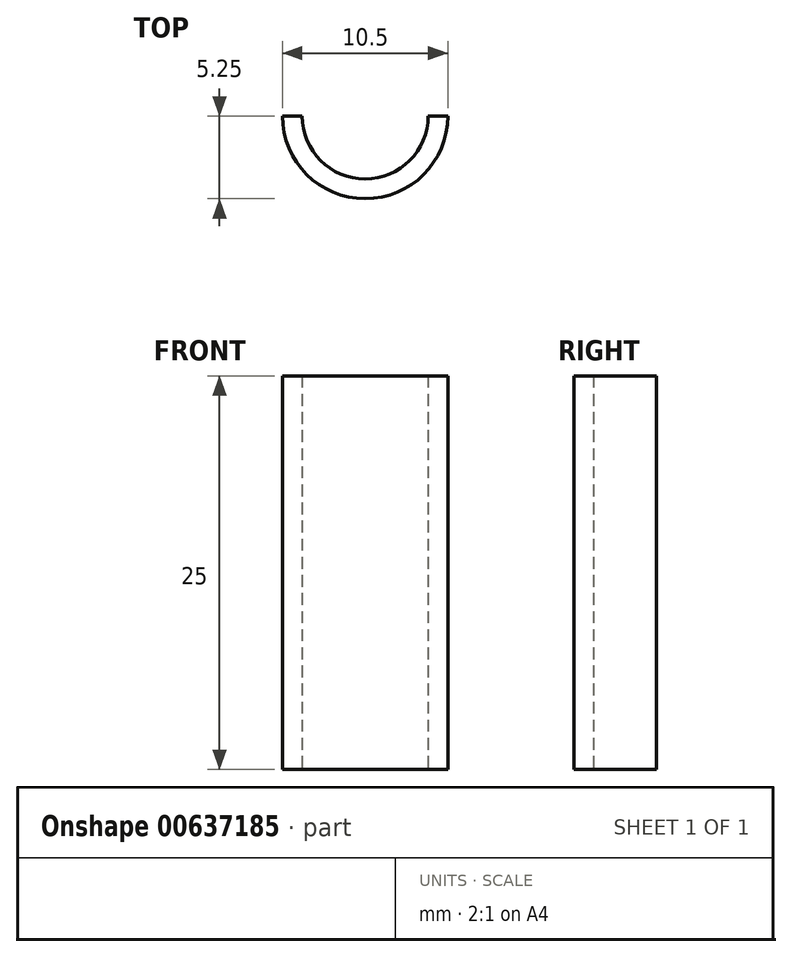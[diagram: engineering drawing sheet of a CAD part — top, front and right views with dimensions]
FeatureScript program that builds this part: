
annotation { "Feature Type Name" : "Feature", "Feature Type Description" : "" }
export const myFeature = defineFeature(function(context is Context, id is Id, definition is map)
    precondition{}
    {
        {
            var Q0;
            Q0=qCreatedBy(makeId("Top.planeOp"),FACE);
            var sketch = newSketch(context, id + "F0", { "sketchPlane" : qUnion([Q0])});
            skArc(sketch, "E0", {"start": v(-4, 0) * mm, "mid": v(0, -4) * mm, "end": v(4, 0) * mm});
            skArc(sketch, "E1", {"start": v(-5.25, 0) * mm, "mid": v(0, -5.25) * mm, "end": v(5.25, 0) * mm});
            skLineSegment(sketch, "E2", {"start": v(-4, 0) * mm, "end": v(-5.25, 0) * mm});
            skLineSegment(sketch, "E3", {"start": v(-5.25, 0) * mm, "end": v(-4, 0) * mm});
            skLineSegment(sketch, "E4", {"start": v(4, 0) * mm, "end": v(5.25, 0) * mm});
            skLineSegment(sketch, "E5", {"start": v(5.25, 0) * mm, "end": v(5.25, -7) * mm});
            skLineSegment(sketch, "E6", {"start": v(-5.25, 0) * mm, "end": v(-5.25, -6.92) * mm});
            skLineSegment(sketch, "E7", {"start": v(-5.25, -6.92) * mm, "end": v(5.25, -7) * mm});
            skSolve(sketch);
        }
        {
            var Q0;
            Q0=makeQuery(id+"F0.imprint","IMPRINT",FACE,{"disambiguationData":[TD([[makeQuery(id+"F0.imprint","IMPRINT",EDGE,{"derivedFrom":sQuery(id+"F0.wireOp",EDGE,"E0")}),-1.0]])]});
            extrude(context, id + "F1", {"entities" : qUnion([Q0]), "depth" : 25 * mm, "offsetDistance" : 25 * mm});
        }
    });
